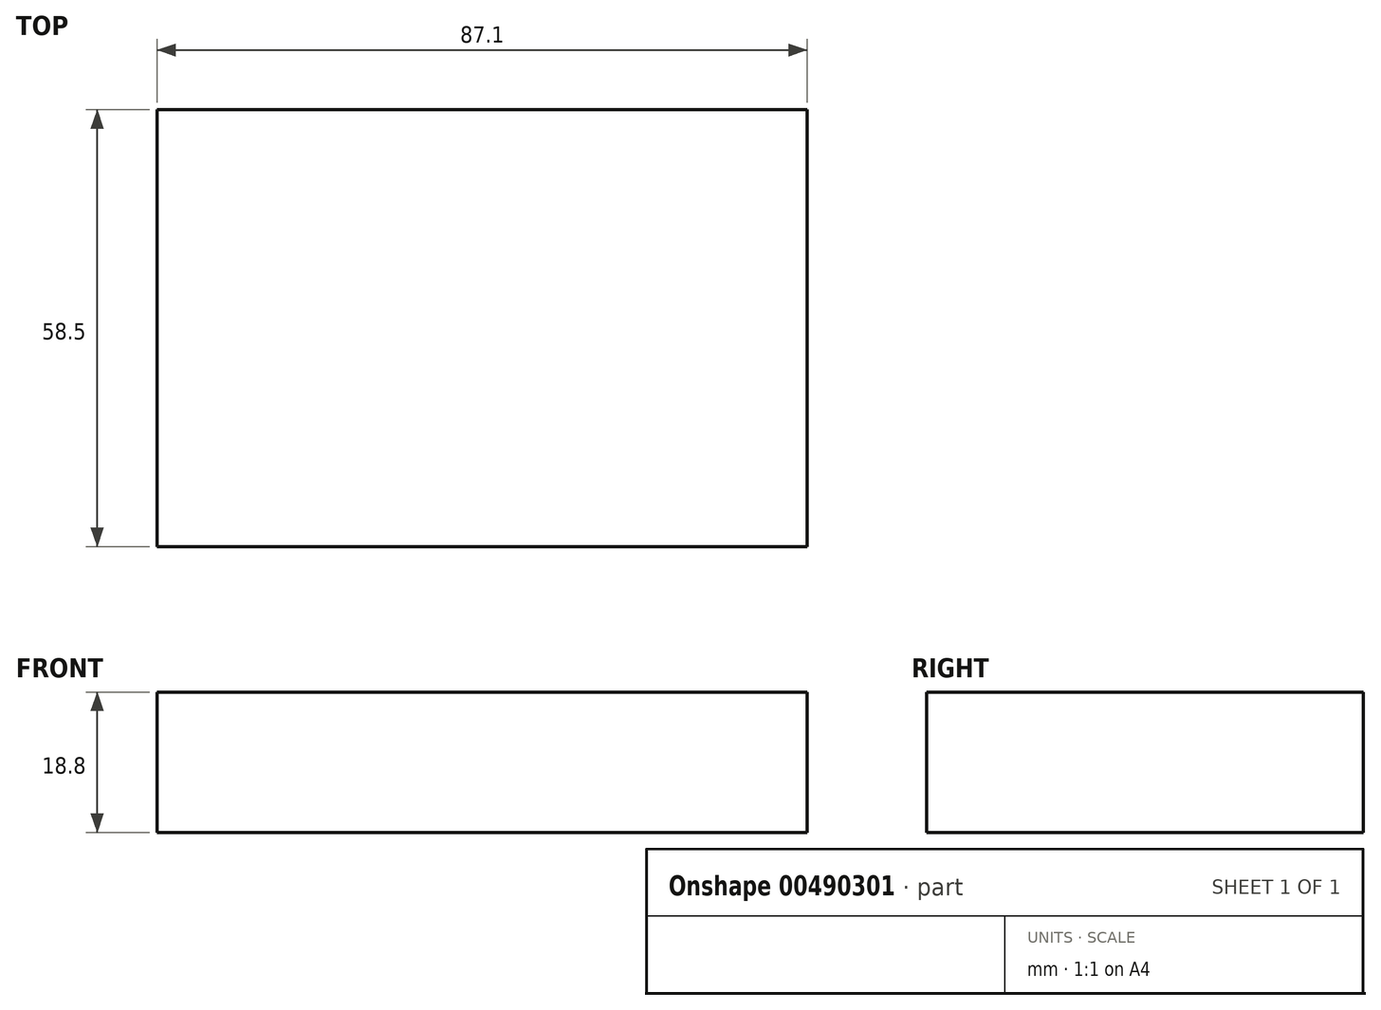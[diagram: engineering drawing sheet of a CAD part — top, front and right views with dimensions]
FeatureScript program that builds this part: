
annotation { "Feature Type Name" : "Feature", "Feature Type Description" : "" }
export const myFeature = defineFeature(function(context is Context, id is Id, definition is map)
    precondition{}
    {
        {
            var Q0;
            Q0=qCreatedBy(makeId("Top.planeOp"),FACE);
            var sketch = newSketch(context, id + "F0", { "sketchPlane" : qUnion([Q0])});
            skLineSegment(sketch, "E0.bottom", {"start": v(-43.55, 29.25) * mm, "end": v(43.55, 29.25) * mm});
            skLineSegment(sketch, "E0.top", {"start": v(-43.55, -29.25) * mm, "end": v(43.55, -29.25) * mm});
            skLineSegment(sketch, "E0.left", {"start": v(-43.55, 29.25) * mm, "end": v(-43.55, -29.25) * mm});
            skLineSegment(sketch, "E0.right", {"start": v(43.55, 29.25) * mm, "end": v(43.55, -29.25) * mm});
            skPoint(sketch, "E0.middle", {"position": v(0, 0) * mm});
            skSolve(sketch);
        }
        {
            var Q0;
            Q0 = qSketchRegion(id + "F0", true);
            extrude(context, id + "F1", {"entities" : qUnion([Q0]), "depth" : 18.8 * mm, "offsetDistance" : 25 * mm});
        }
    });
